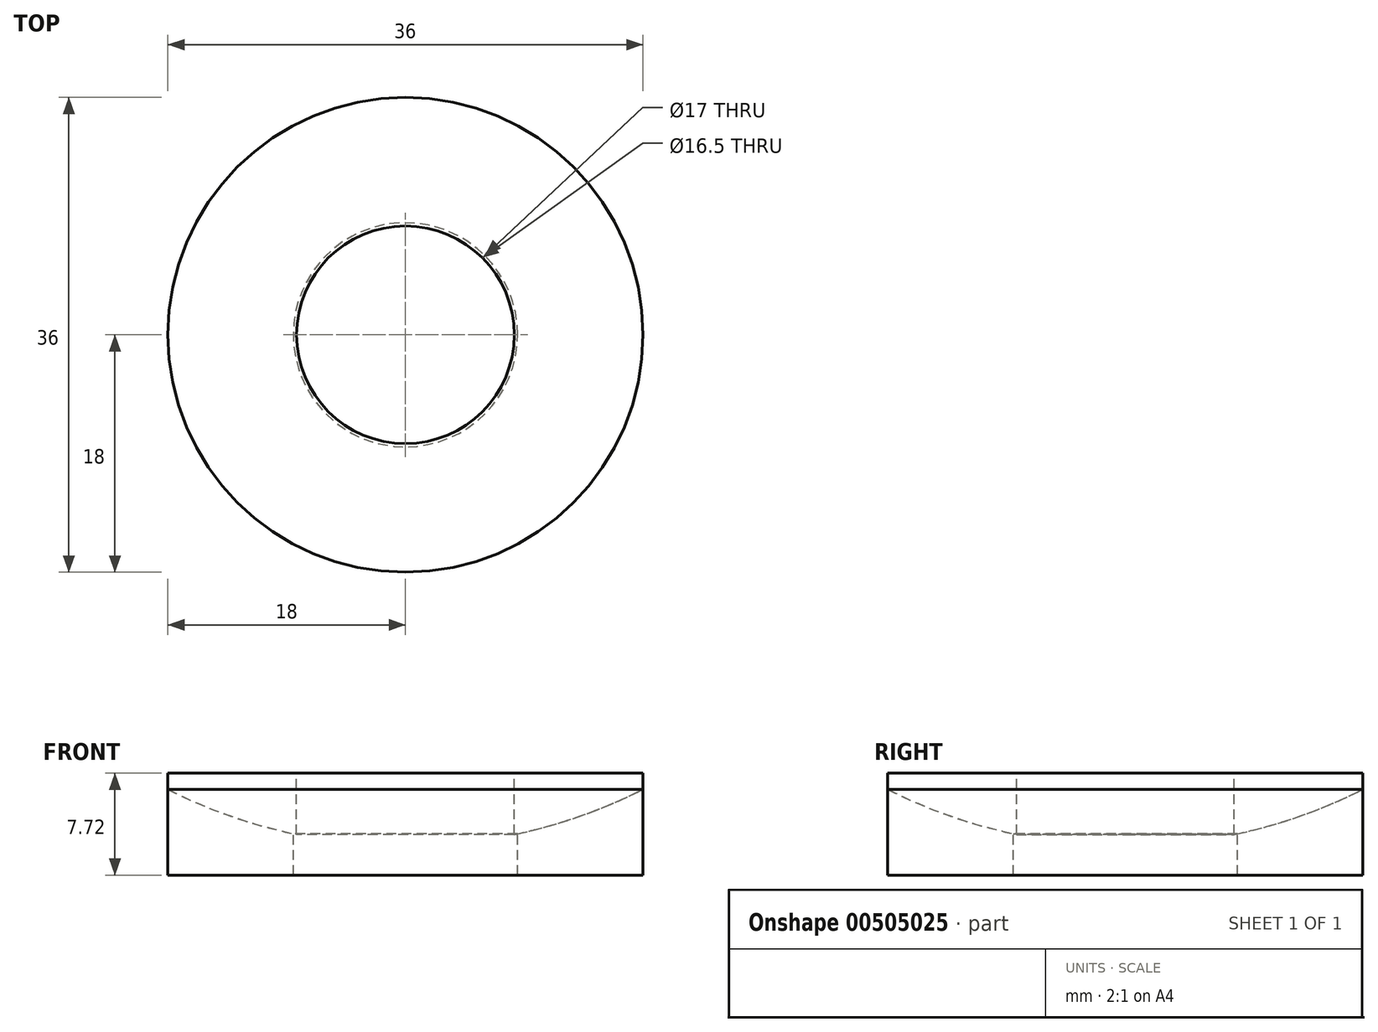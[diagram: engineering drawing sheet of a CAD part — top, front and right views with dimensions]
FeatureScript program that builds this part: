
annotation { "Feature Type Name" : "Feature", "Feature Type Description" : "" }
export const myFeature = defineFeature(function(context is Context, id is Id, definition is map)
    precondition{}
    {
        {
            var Q0;
            Q0=qCreatedBy(makeId("Front.planeOp"),FACE);
            var sketch = newSketch(context, id + "F0", { "sketchPlane" : qUnion([Q0])});
            skLineSegment(sketch, "E0", {"start": v(-20.24, 5.5) * mm, "end": v(63.82, 5.5) * mm});
            skLineSegment(sketch, "E1", {"start": v(-8.25, 5.5) * mm, "end": v(-8.25, 0.86) * mm});
            skLineSegment(sketch, "E2", {"start": v(-18, 5.5) * mm, "end": v(-18, 4.28) * mm});
            skLineSegment(sketch, "E3", {"start": v(0, 40) * mm, "end": v(0, 0) * mm});
            skArc(sketch, "E4", {"start": v(-8.25, 0.86) * mm, "mid": v(-14.43, 2.7) * mm, "end": v(-20.24, 5.5) * mm});
            skSolve(sketch);
        }
        {
            var Q0;
            {var subQ0=sQuery(id+"F0.wireOp",EDGE,"E1");Q0=makeQuery(id+"F0.imprint","IMPRINT",FACE,{"disambiguationData":[TD([[makeQuery(id+"F0.imprint","IMPRINT",EDGE,{"derivedFrom":subQ0}),-1.0]])]});}
            var Q1;
            Q1=sQuery(id+"F0.wireOp",EDGE,"E3");
            revolve(context, id + "F1", {"entities" : qUnion([Q0]), "axis" : qUnion([Q1]), "revolveType" : RevolveType.FULL});
        }
        {
            var Q0;
            Q0=qCreatedBy(makeId("Front.planeOp"),FACE);
            var sketch = newSketch(context, id + "F2", { "sketchPlane" : qUnion([Q0])});
            skLineSegment(sketch, "E5", {"start": v(-18, 4.28) * mm, "end": v(-18, -2.22) * mm});
            skLineSegment(sketch, "E6", {"start": v(-8.5, 0.91) * mm, "end": v(-8.5, -2.22) * mm});
            skLineSegment(sketch, "E7", {"start": v(0, 40) * mm, "end": v(0, -29.27) * mm});
            skLineSegment(sketch, "E8", {"start": v(-18, -2.22) * mm, "end": v(-8.5, -2.22) * mm});
            skArc(sketch, "E9", {"start": v(-8.5, 0.91) * mm, "mid": v(-13.36, 2.3) * mm, "end": v(-18, 4.28) * mm});
            skSolve(sketch);
        }
        {
            var Q0;
            Q0=makeQuery(id+"F2.imprint","IMPRINT",FACE,{"disambiguationData":[TD([[makeQuery(id+"F2.imprint","IMPRINT",EDGE,{"derivedFrom":sQuery(id+"F2.wireOp",EDGE,"E5")}),1.0]])]});
            var Q1;
            Q1=sQuery(id+"F2.wireOp",EDGE,"E7");
            revolve(context, id + "F3", {"entities" : qUnion([Q0]), "axis" : qUnion([Q1]), "revolveType" : RevolveType.FULL});
        }
    });
